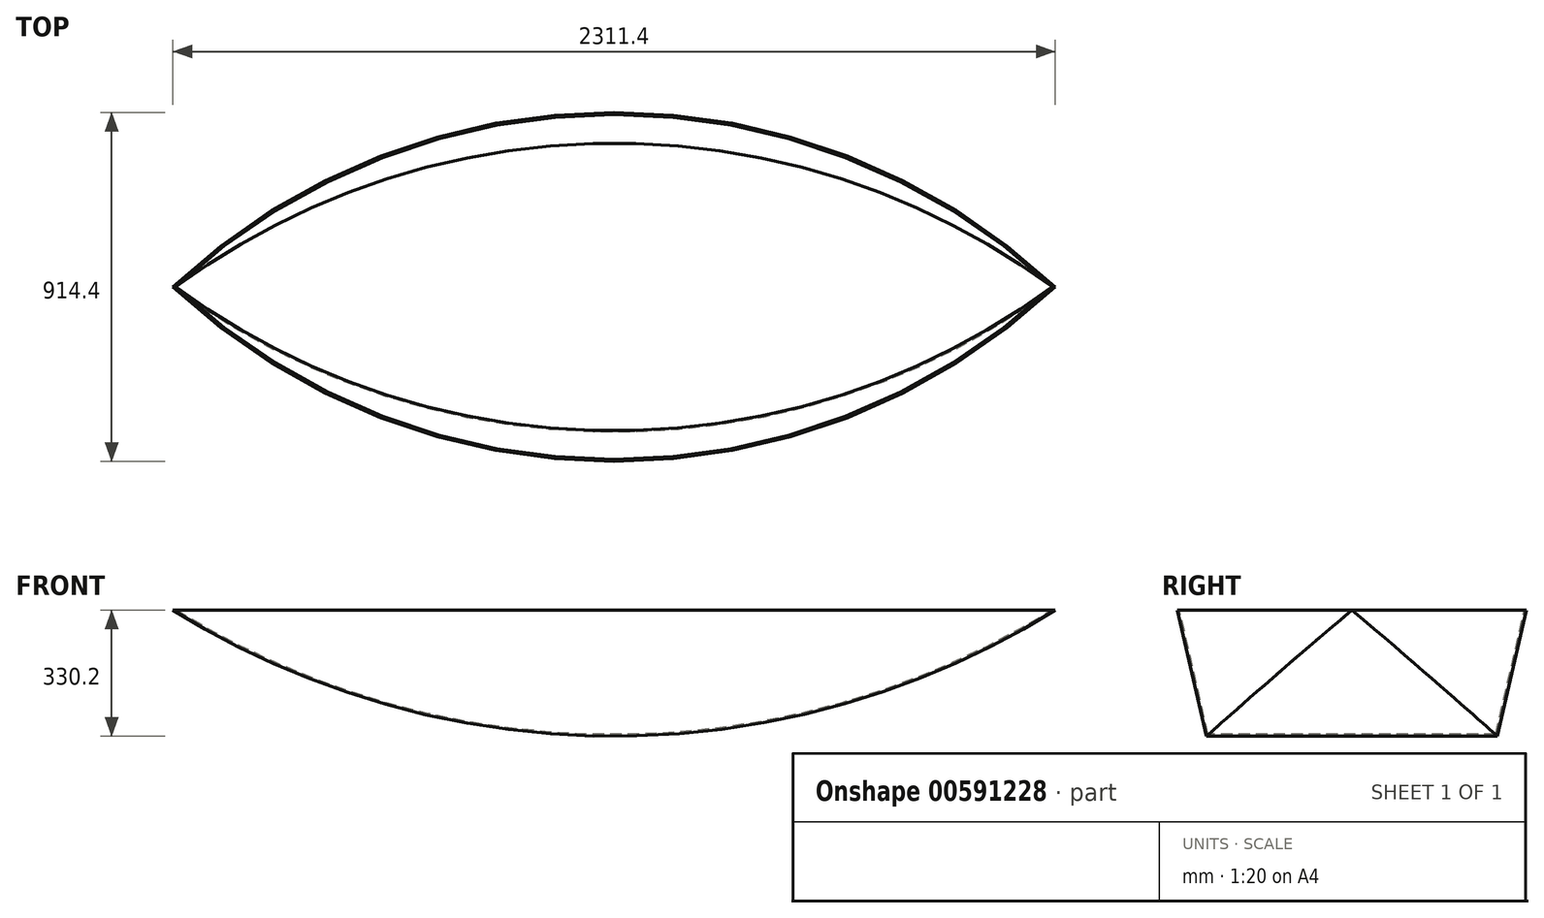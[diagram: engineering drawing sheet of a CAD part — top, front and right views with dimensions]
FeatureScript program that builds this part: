
annotation { "Feature Type Name" : "Feature", "Feature Type Description" : "" }
export const myFeature = defineFeature(function(context is Context, id is Id, definition is map)
    precondition{}
    {
        {
            var Q0;
            Q0=qCreatedBy(makeId("Top.planeOp"),FACE);
            var sketch = newSketch(context, id + "F0", { "sketchPlane" : qUnion([Q0])});
            skArc(sketch, "E0", {"start": v(1155.7, 457.2) * mm, "mid": v(0, 914.4) * mm, "end": v(-1155.7, 457.2) * mm});
            skArc(sketch, "E1", {"start": v(-1155.7, 457.2) * mm, "mid": v(0, 0) * mm, "end": v(1155.7, 457.2) * mm});
            skPoint(sketch, "E2", {"position": v(0, 0) * mm});
            skLineSegment(sketch, "E3", {"start": v(-1155.7, 457.2) * mm, "end": v(1155.7, 457.2) * mm});
            skSolve(sketch);
        }
        {
            var Q0;
            Q0 = qSketchRegion(id + "F0", true);
            extrude(context, id + "F1", {"entities" : qUnion([Q0]), "oppositeDirection" : true, "depth" : 330.2 * mm, "offsetDistance" : 25.4 * mm});
        }
        {
            var Q0;
            Q0=qCreatedBy(makeId("Front.planeOp"),FACE);
            var sketch = newSketch(context, id + "F2", { "sketchPlane" : qUnion([Q0])});
            skLineSegment(sketch, "E4.0", {"start": v(-1155.7, 0) * mm, "end": v(1155.7, 0) * mm});
            skArc(sketch, "E5", {"start": v(-1155.7, 0) * mm, "mid": v(0, -330.2) * mm, "end": v(1155.7, 0) * mm});
            skPoint(sketch, "E6", {"position": v(0, -330.2) * mm});
            skLineSegment(sketch, "E7.bottom", {"start": v(-1282.7, 127) * mm, "end": v(1282.7, 127) * mm});
            skLineSegment(sketch, "E7.top", {"start": v(-1282.7, -457.2) * mm, "end": v(1282.7, -457.2) * mm});
            skLineSegment(sketch, "E7.left", {"start": v(-1282.7, 127) * mm, "end": v(-1282.7, -457.2) * mm});
            skLineSegment(sketch, "E7.right", {"start": v(1282.7, 127) * mm, "end": v(1282.7, -457.2) * mm});
            skSolve(sketch);
        }
        {
            var Q0;
            Q0 = qSketchRegion(id + "F2", true);
            extrude(context, id + "F3", {"entities" : qUnion([Q0]), "operationType" : NewBodyOperationType.REMOVE, "oppositeDirection" : true, "depth" : 1270 * mm, "offsetDistance" : 25.4 * mm});
        }
        {
            var Q0;
            Q0=makeQuery(id+"F1.opExtrude","CAP_FACE",FACE,{"disambiguationData":[OSD([sQuery(id+"F0.wireOp",EDGE,"E0"),sQuery(id+"F0.wireOp",EDGE,"E1")])],"isStart":true});
            var sketch = newSketch(context, id + "F4", { "sketchPlane" : qUnion([Q0])});
            skLineSegment(sketch, "E8.bottom", {"start": v(-1409.7, 1041.4) * mm, "end": v(1409.7, 1041.4) * mm});
            skLineSegment(sketch, "E8.top", {"start": v(-1409.7, -127) * mm, "end": v(1409.7, -127) * mm});
            skLineSegment(sketch, "E8.left", {"start": v(-1409.7, 1041.4) * mm, "end": v(-1409.7, -127) * mm});
            skLineSegment(sketch, "E8.right", {"start": v(1409.7, 1041.4) * mm, "end": v(1409.7, -127) * mm});
            skArc(sketch, "E9.0", {"start": v(1155.7, 457.2) * mm, "mid": v(0, 914.4) * mm, "end": v(-1155.7, 457.2) * mm});
            skArc(sketch, "E10.0", {"start": v(-1155.7, 457.2) * mm, "mid": v(0, 0) * mm, "end": v(1155.7, 457.2) * mm});
            skSolve(sketch);
        }
        {
            var Q0;
            Q0 = qSketchRegion(id + "F4", true);
            extrude(context, id + "F5", {"entities" : qUnion([Q0]), "operationType" : NewBodyOperationType.REMOVE, "oppositeDirection" : true, "depth" : 1016 * mm, "offsetDistance" : 25.4 * mm, "hasDraft" : true, "draftAngle" : 13 * degree});
        }
        {
            var Q0;
            Q0=makeQuery(id+"F1.opExtrude","CAP_FACE",FACE,{"disambiguationData":[OSD([sQuery(id+"F0.wireOp",EDGE,"E0"),sQuery(id+"F0.wireOp",EDGE,"E1")])],"isStart":true});
            shell(context, id + "F6", {"entities" : qUnion([Q0]), "thickness" : 5.16 * mm});
        }
    });
